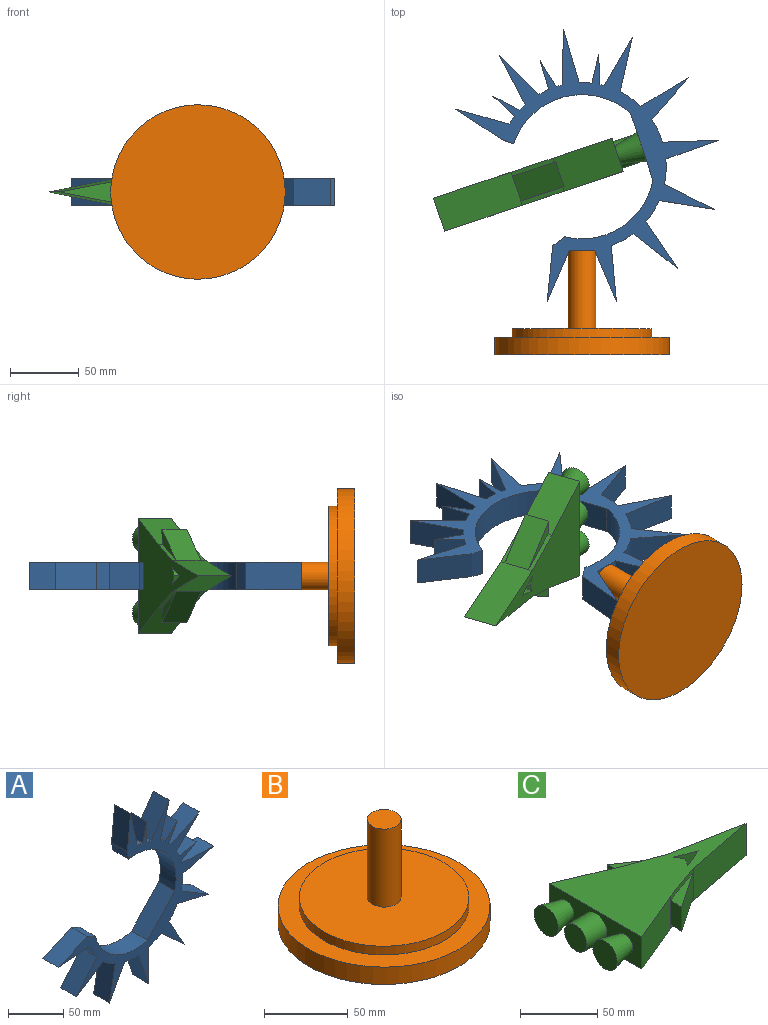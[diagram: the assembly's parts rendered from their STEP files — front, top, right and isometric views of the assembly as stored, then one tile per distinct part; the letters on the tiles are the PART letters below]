
ASSEMBLY  parts=3 mates=2
PART A: 45 faces, bbox 198.9x20.3x200.6 mm
  f0: plane 37.63x20.32mm, normal (-0.37,0,0.93), area 824.7mm2, adj f1,f42,f43,f44
  f1: plane 40.53x20.32mm, normal (0.08,0,-1), area 825.9mm2, adj f0,f2,f43,f44
  f2: plane 20.32x16.2mm, normal (-0.88,0,-0.47), area 372.4mm2, adj f1,f3,f43,f44
  f3: plane 31.5x25.59mm, normal (-0.78,0,0.63), area 824.7mm2, adj f2,f4,f43,f44
  f4: plane 34.01x22.26mm, normal (0.55,0,-0.84), area 825.9mm2, adj f3,f5,f43,f44
  f5: cylinder r=61.32mm len=20.32mm, axis (0,1,0), area 373.8mm2, adj f4,f6,f43,f44
  f6: plane 39.95x20.32mm, normal (-0.98,0,0.18), area 824.7mm2, adj f5,f7,f43,f44
  f7: plane 35.92x20.32mm, normal (0.88,0,-0.47), area 825.9mm2, adj f6,f8,f43,f44
  f8: cylinder r=61.32mm len=20.32mm, axis (0,1,0), area 373.8mm2, adj f7,f9,f43,f44
  f9: plane 38.45x20.32mm, normal (-0.95,0,-0.32), area 824.7mm2, adj f8,f10,f43,f44
  f10: plane 40.64x20.32mm, normal (1,0,0.02), area 825.9mm2, adj f9,f11,f43,f44
  f11: cylinder r=61.32mm len=20.32mm, axis (0,1,0), area 373.8mm2, adj f10,f12,f43,f44
  f12: plane 29.96x27.38mm, normal (-0.67,0,-0.74), area 824.7mm2, adj f11,f13,f43,f44
  f13: plane 35.24x20.32mm, normal (0.87,0,0.5), area 825.9mm2, adj f12,f14,f43,f44
  f14: cylinder r=61.32mm len=20.32mm, axis (0,1,0), area 373.8mm2, adj f13,f15,f43,f44
  f15: plane 39.46x20.32mm, normal (-0.23,0,-0.97), area 824.7mm2, adj f14,f16,f43,f44
  f16: plane 34.75x21.08mm, normal (0.52,0,0.86), area 825.9mm2, adj f15,f17,f43,f44
  f17: cylinder r=61.32mm len=20.32mm, axis (0,1,0), area 373.8mm2, adj f16,f18,f43,f44
  f18: plane 39.14x20.32mm, normal (0.26,0,-0.96), area 824.7mm2, adj f17,f19,f43,f44
  f19: plane 40.61x20.32mm, normal (0.04,0,1), area 825.9mm2, adj f18,f20,f43,f44
  f20: cylinder r=61.32mm len=20.32mm, axis (0,1,0), area 66.8mm2, adj f19,f21,f43,f44
  f21: plane 20.32x19.09mm, normal (0.5,0,-0.87), area 447.9mm2, adj f20,f22,f43,f44
  f22: plane 20.92x20.32mm, normal (-0.25,0,0.97), area 439.6mm2, adj f21,f23,f43,f44
  f23: cylinder r=61.32mm len=20.32mm, axis (0,1,0), area 189.1mm2, adj f22,f24,f43,f44
  f24: plane 29.08x28.32mm, normal (0.7,0,-0.72), area 824.7mm2, adj f23,f25,f43,f44
  f25: plane 36.36x20.32mm, normal (-0.45,0,0.89), area 825.9mm2, adj f24,f26,f43,f44
  f26: cylinder r=61.32mm len=20.32mm, axis (0,1,0), area 90.9mm2, adj f25,f27,f43,f44
  f27: plane 20.32x19.09mm, normal (0.87,0,-0.5), area 447.9mm2, adj f26,f28,f43,f44
  f28: plane 20.32x15.36mm, normal (-0.7,0,0.71), area 439.6mm2, adj f27,f29,f43,f44
  f29: cylinder r=61.32mm len=20.32mm, axis (0,1,0), area 164.9mm2, adj f28,f30,f43,f44
  f30: plane 38.84x20.32mm, normal (0.96,0,-0.29), area 824.7mm2, adj f29,f31,f43,f44
  f31: plane 33.47x23.06mm, normal (-0.82,0,0.57), area 825.9mm2, adj f30,f32,f43,f44
  f32: cylinder r=61.32mm len=20.32mm, axis (0,1,0), area 115.1mm2, adj f31,f33,f43,f44
  f33: plane 22.04x20.32mm, normal (1,0,0), area 447.9mm2, adj f32,f34,f43,f44
  f34: plane 20.88x20.32mm, normal (-0.96,0,0.26), area 439.6mm2, adj f33,f35,f43,f44
  f35: cylinder r=61.32mm len=20.32mm, axis (0,1,0), area 140.7mm2, adj f34,f36,f43,f44
  f36: plane 39.7x20.32mm, normal (0.98,0,0.21), area 824.7mm2, adj f35,f37,f43,f44
  f37: plane 40.44x20.32mm, normal (-1,0,0.1), area 825.9mm2, adj f36,f38,f43,f44
  f38: plane 20.32x8.69mm, normal (-0.99,0,-0.16), area 178.9mm2, adj f37,f39,f43,f44
  f39: cylinder r=52.52mm len=65.66mm, axis (0,1,0), area 2118.9mm2, adj f38,f40,f43,f44
  f40: plane 37.01x35.26mm, normal (-0.72,0,0.69), area 1038.7mm2, adj f39,f41,f43,f44
  f41: cylinder r=52.52mm len=66.58mm, axis (0,1,0), area 1740.2mm2, adj f40,f42,f43,f44
  f42: plane 20.32x9.79mm, normal (0.42,0,0.91), area 218.7mm2, adj f0,f41,f43,f44
  f43: plane 200.56x198.86mm, normal (0,-1,0), area 5240.5mm2, adj f0,f1,f2,f3,f4,f5,f6,f7
  f44: plane 200.56x198.86mm, normal (0,1,0), area 5240.5mm2, adj f0,f1,f2,f3,f4,f5,f6,f7
PART B: 7 faces, bbox 127x127x76.2 mm
  f0: cylinder r=50.8mm len=101.6mm, axis (0,0,-1), area 2026.8mm2, adj f1,f4
  f1: plane 101.6x101.6mm, normal (0,0,1), area 7783mm2, adj f0,f5
  f2: plane 127x127mm, normal (0,0,-1), area 12667.7mm2, adj f3
  f3: cylinder r=63.5mm len=127mm, axis (0,0,-1), area 5067.1mm2, adj f2,f4
  f4: plane 127x127mm, normal (0,0,1), area 4560.4mm2, adj f0,f3
  f5: cylinder r=10.16mm len=57.15mm, axis (0,0,-1), area 3648.3mm2, adj f1,f6
  f6: plane 20.32x20.32mm, normal (0,0,1), area 324.3mm2, adj f5
PART C: 29 faces, bbox 155.6x84.3x25.4 mm
  f0: plane 32.18x11.64mm, normal (0.34,-0.94,0), area 108.7mm2, adj f3,f5,f14,f22
  f1: plane 32.18x11.64mm, normal (0.34,0.94,0), area 108.7mm2, adj f6,f12,f14,f18
  f2: plane 84.29x25.4mm, normal (-1,0,0), area 1517.3mm2, adj f3,f12,f13,f14,f23,f25,f27
  f3: plane 45.4x25.4mm, normal (0.39,-0.92,0), area 1251.2mm2, adj f0,f2,f4,f13,f14,f19
  f4: plane 32.18x11.64mm, normal (0.34,-0.94,0), area 108.7mm2, adj f3,f5,f13,f21
  f5: plane 59.55x25.4mm, normal (0.19,-0.98,0), area 1540mm2, adj f0,f4,f6,f13,f14,f20
  f6: plane 59.55x25.4mm, normal (0.19,0.98,0), area 1540mm2, adj f1,f5,f7,f13,f14,f16
  f7: plane 32.18x11.64mm, normal (0.34,0.94,0), area 108.7mm2, adj f6,f12,f13,f17
  f8: plane 25.4x16.09mm, normal (-0.37,-0.93,0), area 439.9mm2, adj f9,f11,f13,f14
  f9: plane 25.4x16.09mm, normal (-0.37,0.93,0), area 439.9mm2, adj f8,f10,f13,f14
  f10: plane 25.4x6.41mm, normal (0.86,-0.51,0), area 188.8mm2, adj f9,f11,f13,f14
  f11: plane 25.4x6.41mm, normal (0.86,0.51,0), area 188.8mm2, adj f8,f10,f13,f14
  f12: plane 45.4x25.4mm, normal (0.39,0.92,0), area 1251.2mm2, adj f1,f2,f7,f13,f14,f15
  f13: plane 137.13x84.29mm, normal (0,0,1), area 4665.1mm2, adj f2,f3,f4,f5,f6,f7,f8,f9
  f14: plane 137.13x84.29mm, normal (0,0,-1), area 4665.1mm2, adj f0,f1,f2,f3,f5,f6,f8,f9
  f15: plane 19.05x10.81mm, normal (-1,-0.09,0), area 206.8mm2, adj f12,f16,f17,f18
  f16: plane 33.14x22.45mm, normal (0.56,0.83,0), area 762.6mm2, adj f6,f15,f17,f18
  f17: plane 33.14x22.45mm, normal (0,0,1), area 168.5mm2, adj f7,f15,f16
  f18: plane 33.14x22.45mm, normal (0,0,-1), area 168.5mm2, adj f1,f15,f16
  f19: plane 19.05x10.81mm, normal (-1,0.09,0), area 206.8mm2, adj f3,f20,f21,f22
  f20: plane 33.14x22.45mm, normal (0.56,-0.83,0), area 762.6mm2, adj f5,f19,f21,f22
  f21: plane 33.14x22.45mm, normal (0,0,1), area 168.5mm2, adj f4,f19,f20
  f22: plane 33.14x22.45mm, normal (0,0,-1), area 168.5mm2, adj f0,f19,f20
  f23: cylinder r=10.16mm len=20.32mm, axis (1,0,0), area 1176.6mm2, adj f2,f24
  f24: plane 20.32x20.32mm, normal (-1,0,0), area 324.3mm2, adj f23
  f25: cone r=6.9mm half-angle=12.7deg, axis (-1,0,0), area 1066.4mm2, adj f2,f26
  f26: plane 22.13x22.13mm, normal (-1,0,0), area 384.6mm2, adj f25
  f27: cone r=6.9mm half-angle=12.7deg, axis (-1,0,0), area 1066.4mm2, adj f2,f28
  f28: plane 22.13x22.13mm, normal (-1,0,0), area 384.6mm2, adj f27
PLACE A rot(axis=(-0.76,-0.46,0.46),105.4deg) t=(27.4,-242.79,-22.14)mm
PLACE B rot(axis=(-1,0,0),90deg) t=(27.4,-379.62,-22.14)mm
PLACE C rot(axis=(-0.11,0.7,-0.7),166.9deg) t=(-20.14,-258.71,-22.14)mm
MATE fastened A.f2 <-> B.f5  axis (0,-1,0) through (27.4,-303.42,-22.14)mm
MATE fastened C.f23 <-> A.f40  axis (0.95,0.32,0) through (70.9,-228.22,-22.14)mm
